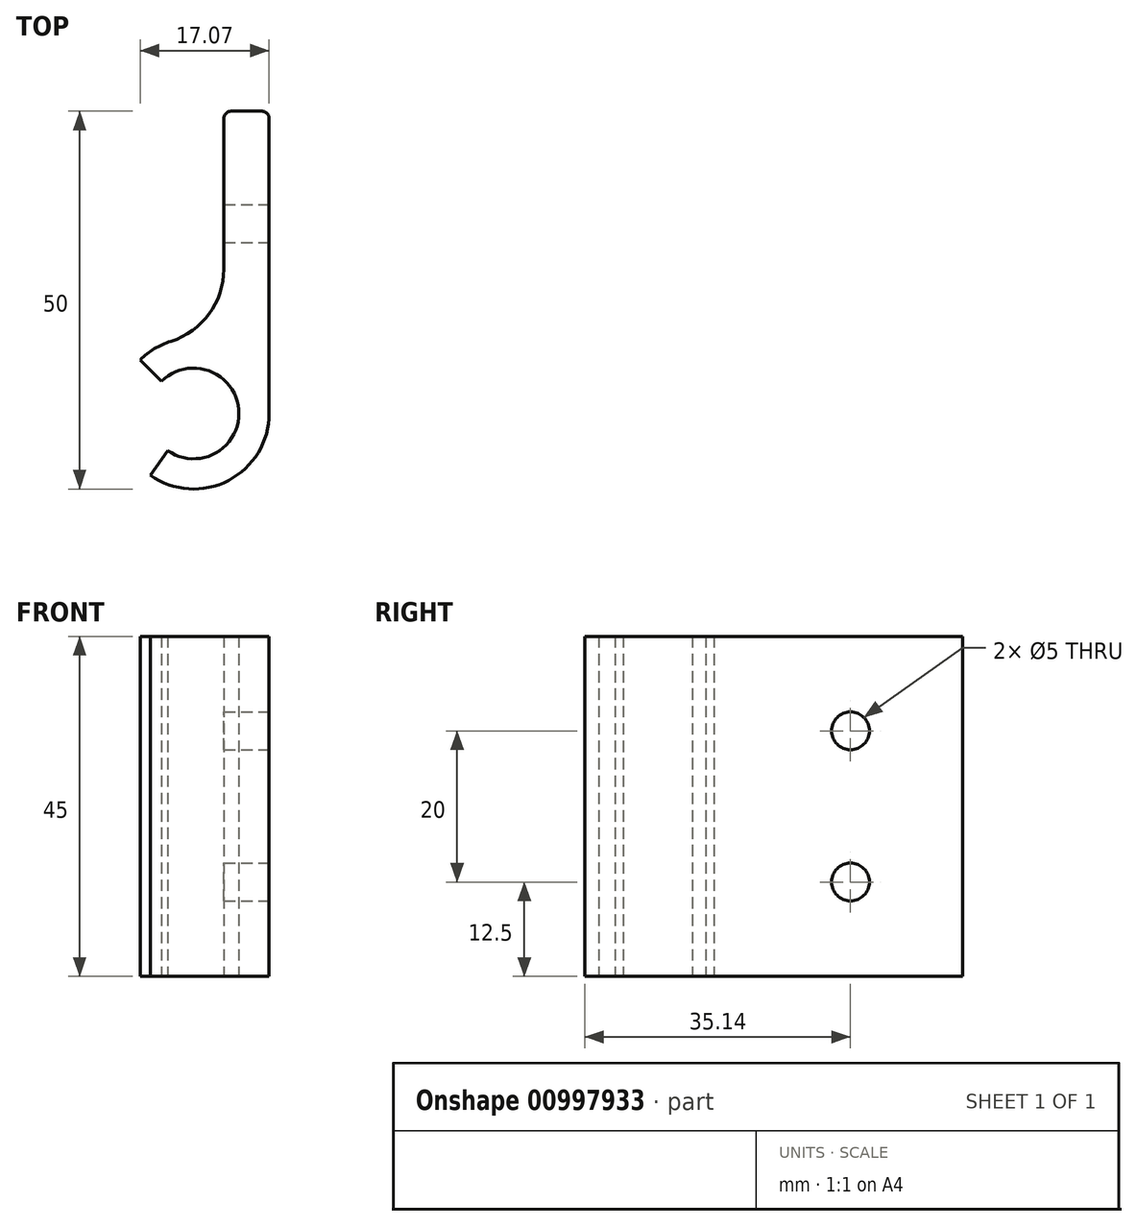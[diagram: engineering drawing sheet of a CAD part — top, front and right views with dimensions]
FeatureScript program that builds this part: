
annotation { "Feature Type Name" : "Feature", "Feature Type Description" : "" }
export const myFeature = defineFeature(function(context is Context, id is Id, definition is map)
    precondition{}
    {
        {
            var Q0;
            Q0=qCreatedBy(makeId("Top.planeOp"),FACE);
            var sketch = newSketch(context, id + "F0", { "sketchPlane" : qUnion([Q0])});
            skArc(sketch, "E0", {"start": v(-3.44, -4.92) * mm, "mid": v(5.98, 0.52) * mm, "end": v(-4.24, 4.24) * mm});
            skArc(sketch, "E1", {"start": v(-3, 9.54) * mm, "mid": v(-5.18, 8.55) * mm, "end": v(-7.07, 7.07) * mm});
            skLineSegment(sketch, "E2", {"start": v(10, 0) * mm, "end": v(10, 39) * mm});
            skLineSegment(sketch, "E3", {"start": v(9, 40) * mm, "end": v(5, 40) * mm});
            skLineSegment(sketch, "E4.trimOffspring", {"start": v(4, 19.08) * mm, "end": v(4, 39) * mm});
            skLineSegment(sketch, "E5", {"start": v(0, 10) * mm, "end": v(-10, 10) * mm, "construction": true});
            skLineSegment(sketch, "E6", {"start": v(0, -10) * mm, "end": v(-7, -10) * mm, "construction": true});
            skLineSegment(sketch, "E7", {"start": v(0, 0) * mm, "end": v(-7, -10) * mm, "construction": true});
            skLineSegment(sketch, "E8", {"start": v(0, 0) * mm, "end": v(-10, 10) * mm, "construction": true});
            skArc(sketch, "E9.trimOffspring", {"start": v(-5.73, -8.2) * mm, "mid": v(4.62, -8.87) * mm, "end": v(10, 0) * mm});
            skPoint(sketch, "E10.visualSharp", {"position": v(4, 9.17) * mm});
            skArc(sketch, "E10.filletArc", {"start": v(-3, 9.54) * mm, "mid": v(2.06, 13.16) * mm, "end": v(4, 19.08) * mm});
            skPoint(sketch, "E11.visualSharp", {"position": v(4, 40) * mm});
            skArc(sketch, "E11.filletArc", {"start": v(5, 40) * mm, "mid": v(4.3, 39.7) * mm, "end": v(4, 39) * mm});
            skPoint(sketch, "E12.visualSharp", {"position": v(10, 40) * mm});
            skArc(sketch, "E12.filletArc", {"start": v(10, 39) * mm, "mid": v(9.7, 39.7) * mm, "end": v(9, 40) * mm});
            skLineSegment(sketch, "E13", {"start": v(-7.07, 7.07) * mm, "end": v(-4.24, 4.24) * mm});
            skLineSegment(sketch, "E14", {"start": v(-5.73, -8.2) * mm, "end": v(-3.44, -4.92) * mm});
            skSolve(sketch);
        }
        {
            var Q0;
            Q0=makeQuery(id+"F0.imprint","IMPRINT",FACE,{"disambiguationData":[TD([[makeQuery(id+"F0.imprint","IMPRINT",EDGE,{"derivedFrom":sQuery(id+"F0.wireOp",EDGE,"E0")}),-1.0]])]});
            extrude(context, id + "F1", {"entities" : qUnion([Q0]), "depth" : 45 * mm, "offsetDistance" : 25 * mm});
        }
        {
            var Q0;
            Q0=qCreatedBy(makeId("Top.planeOp"),FACE);
            var sketch = newSketch(context, id + "F2", { "sketchPlane" : qUnion([Q0])});
            skLineSegment(sketch, "E15", {"start": v(0, 0) * mm, "end": v(0, 25) * mm});
            skLineSegment(sketch, "E16", {"start": v(0, 25) * mm, "end": v(10.62, 25) * mm});
            skLineSegment(sketch, "E17.0.0", {"start": v(4, 39) * mm, "end": v(4, 19.08) * mm});
            skLineSegment(sketch, "E17.0.2", {"start": v(4, 19.08) * mm, "end": v(4, 39) * mm});
            skSolve(sketch);
        }
        {
            var Q0;
            Q0=makeQuery(id+"F1.opExtrude","SWEPT_FACE",FACE,{"disambiguationData":[OSD([sQuery(id+"F0.wireOp",EDGE,"E2")])]});
            var sketch = newSketch(context, id + "F3", { "sketchPlane" : qUnion([Q0])});
            skLineSegment(sketch, "E18", {"start": v(25.14, 0) * mm, "end": v(25.14, 45) * mm, "construction": true});
            skLineSegment(sketch, "E19.0", {"start": v(39, 12.5) * mm, "end": v(19.08, 12.5) * mm, "construction": true});
            skLineSegment(sketch, "E20.0", {"start": v(39, 32.5) * mm, "end": v(19.08, 32.5) * mm, "construction": true});
            skCircle(sketch, "E21", {"center": v(25.14, 32.5) * mm, "radius": 2.5 * mm});
            skCircle(sketch, "E22", {"center": v(25.14, 12.5) * mm, "radius": 2.5 * mm});
            skSolve(sketch);
        }
        {
            var Q0;
            Q0=makeQuery(id+"F3.imprint","IMPRINT",FACE,{"disambiguationData":[TD([[makeQuery(id+"F3.imprint","IMPRINT",EDGE,{"derivedFrom":sQuery(id+"F3.wireOp",EDGE,"E21")}),1.0]])]});
            var Q1;
            Q1=makeQuery(id+"F3.imprint","IMPRINT",FACE,{"disambiguationData":[TD([[makeQuery(id+"F3.imprint","IMPRINT",EDGE,{"derivedFrom":sQuery(id+"F3.wireOp",EDGE,"E22")}),1.0]])]});
            extrude(context, id + "F4", {"entities" : qUnion([Q0, Q1]), "operationType" : NewBodyOperationType.REMOVE, "oppositeDirection" : true, "depth" : 6 * mm, "offsetDistance" : 25 * mm});
        }
    });
